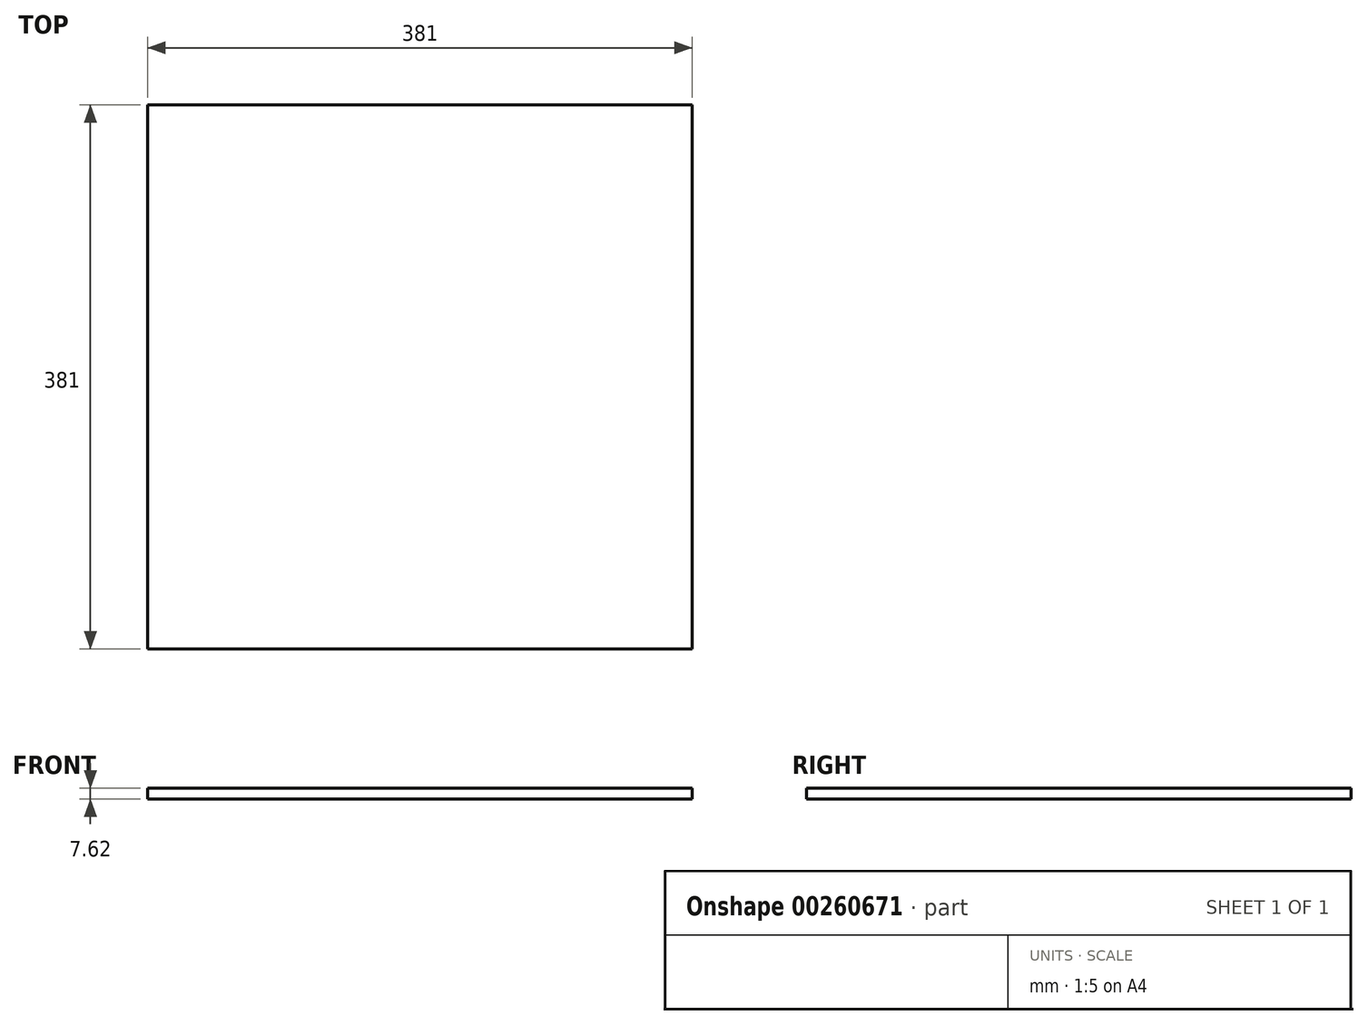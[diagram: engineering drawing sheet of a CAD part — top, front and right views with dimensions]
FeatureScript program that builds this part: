
annotation { "Feature Type Name" : "Feature", "Feature Type Description" : "" }
export const myFeature = defineFeature(function(context is Context, id is Id, definition is map)
    precondition{}
    {
        {
            var Q0;
            Q0=qCreatedBy(makeId("Top.planeOp"),FACE);
            var sketch = newSketch(context, id + "F0", { "sketchPlane" : qUnion([Q0])});
            skLineSegment(sketch, "E0.bottom", {"start": v(-199.96, 197.05) * mm, "end": v(181.04, 197.05) * mm});
            skLineSegment(sketch, "E0.top", {"start": v(-199.96, -183.95) * mm, "end": v(181.04, -183.95) * mm});
            skLineSegment(sketch, "E0.left", {"start": v(-199.96, 197.05) * mm, "end": v(-199.96, -183.95) * mm});
            skLineSegment(sketch, "E0.right", {"start": v(181.04, 197.05) * mm, "end": v(181.04, -183.95) * mm});
            skSolve(sketch);
        }
        {
            var Q0;
            Q0=makeQuery(id+"F0.imprint","IMPRINT",FACE,{"disambiguationData":[TD([[makeQuery(id+"F0.imprint","IMPRINT",EDGE,{"derivedFrom":sQuery(id+"F0.wireOp",EDGE,"E0.bottom")}),-1.0]])]});
            extrude(context, id + "F1", {"entities" : qUnion([Q0]), "depth" : 7.62 * mm});
        }
    });
